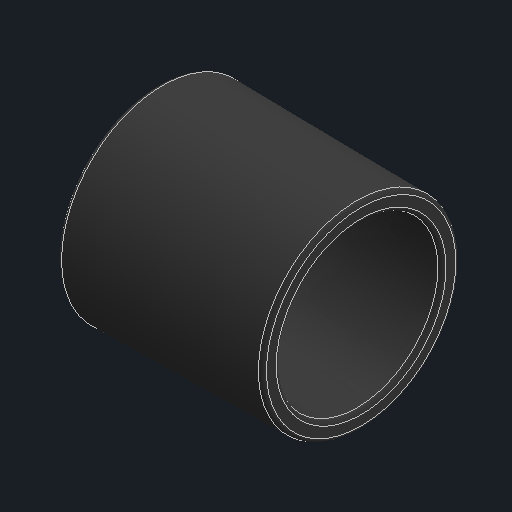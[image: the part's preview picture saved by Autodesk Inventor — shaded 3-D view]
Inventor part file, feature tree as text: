
AUTODESK INVENTOR PART (.ipt)
format: ipt  version: 2025 (Build 290162010, 162A)  size: 150,016 bytes
history: native  units: mm
features: revolve x1, sketch x1
ambient origin geometry x8: Origin, YZ Plane, XZ Plane, XY Plane, X Axis, Y Axis, Z Axis, Center Point
bodies: Solid1 (feature_tree)
feature tree (2):
  revolve  "Revolution1"  [1 undecoded]
  sketch  "Sketch1"  dims[d0=13.0mm d1=11.0mm d2=5.0mm d3=1.1mm d5=2.0mm d6=6.25mm d7=60.0mm d8=0.5mm d9=0.25mm d10=90.0deg d11=0.872665mm]
note: 1 required parameter value undecoded (feature->parameter linkage not recoverable at this tier; creation-order binding heuristic only, values carry confidence <= 0.55)
